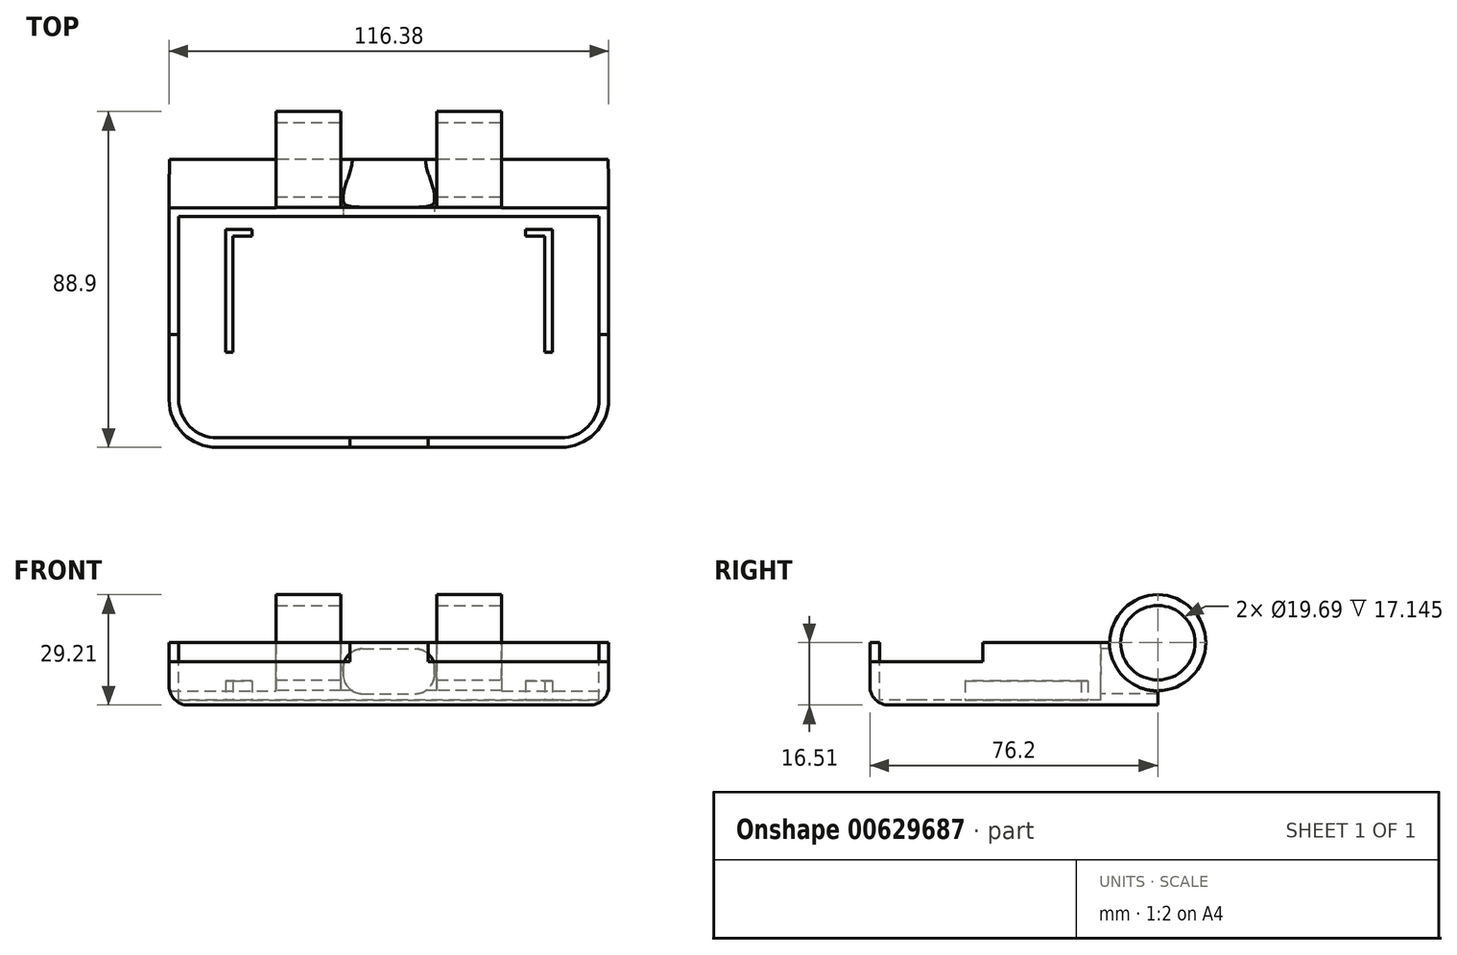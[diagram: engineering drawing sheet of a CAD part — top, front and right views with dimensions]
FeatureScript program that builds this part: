
annotation { "Feature Type Name" : "Feature", "Feature Type Description" : "" }
export const myFeature = defineFeature(function(context is Context, id is Id, definition is map)
    precondition{}
    {
        {
            var Q0;
            Q0=qCreatedBy(makeId("Top.planeOp"),FACE);
            var sketch = newSketch(context, id + "F0", { "sketchPlane" : qUnion([Q0])});
            skLineSegment(sketch, "E0.bottom", {"start": v(58.2, 38.1) * mm, "end": v(-58.2, 38.1) * mm});
            skLineSegment(sketch, "E0.top", {"start": v(58.2, -38.1) * mm, "end": v(-58.2, -38.1) * mm});
            skLineSegment(sketch, "E0.left", {"start": v(58.2, 38.1) * mm, "end": v(58.2, -38.1) * mm});
            skLineSegment(sketch, "E0.right", {"start": v(-58.2, 38.1) * mm, "end": v(-58.2, -38.1) * mm});
            skPoint(sketch, "E0.middle", {"position": v(0, 0) * mm});
            skSolve(sketch);
        }
        {
            var Q0;
            Q0 = qSketchRegion(id + "F0", true);
            extrude(context, id + "F1", {"entities" : qUnion([Q0]), "oppositeDirection" : true, "depth" : 16.5 * mm, "offsetDistance" : 25.4 * mm});
        }
        {
            var Q0;
            Q0=qCreatedBy(makeId("Right.planeOp"),FACE);
            var sketch = newSketch(context, id + "F2", { "sketchPlane" : qUnion([Q0])});
            skCircle(sketch, "E1", {"center": v(38.1, 0) * mm, "radius": 12.7 * mm});
            skSolve(sketch);
        }
        {
            var Q0;
            Q0 = qSketchRegion(id + "F2", true);
            extrude(context, id + "F3", {"entities" : qUnion([Q0]), "operationType" : NewBodyOperationType.ADD, "endBound" : BoundingType.SYMMETRIC, "depth" : 127 * mm, "offsetDistance" : 25.4 * mm});
        }
        {
            var Q0;
            Q0=makeQuery(id+"F1.opExtrude","SWEPT_EDGE",EDGE,{"disambiguationData":[OSD([sQuery(id+"F0.wireOp",EDGE,"E0.top"),sQuery(id+"F0.wireOp",EDGE,"E0.right")])]});
            var Q1;
            Q1=makeQuery(id+"F1.opExtrude","SWEPT_EDGE",EDGE,{"disambiguationData":[OSD([sQuery(id+"F0.wireOp",EDGE,"E0.top"),sQuery(id+"F0.wireOp",EDGE,"E0.left")])]});
            fillet(context, id + "F4", {"entities" : qUnion([Q0, Q1]), "radius" : 12.7 * mm, "tangentPropagation" : true, "allowEdgeOverflow" : false});
        }
        {
            var Q0;
            Q0=qCreatedBy(makeId("Top.planeOp"),FACE);
            var sketch = newSketch(context, id + "F5", { "sketchPlane" : qUnion([Q0])});
            skLineSegment(sketch, "E2.0", {"start": v(63.5, 50.8) * mm, "end": v(63.5, 25.4) * mm, "construction": true});
            skLineSegment(sketch, "E3", {"start": v(-63.5, 38.1) * mm, "end": v(0, 38.1) * mm});
            skLineSegment(sketch, "E4", {"start": v(0, 38.1) * mm, "end": v(63.5, 38.1) * mm});
            skLineSegment(sketch, "E5", {"start": v(63.5, 38.1) * mm, "end": v(63.5, 50.86) * mm});
            skLineSegment(sketch, "E6", {"start": v(63.5, 50.86) * mm, "end": v(29.85, 50.86) * mm});
            skLineSegment(sketch, "E7", {"start": v(29.85, 50.86) * mm, "end": v(29.85, 47.94) * mm});
            skLineSegment(sketch, "E8", {"start": v(29.85, 47.94) * mm, "end": v(0, 47.94) * mm});
            skLineSegment(sketch, "E9", {"start": v(0, 47.94) * mm, "end": v(-29.85, 47.94) * mm});
            skLineSegment(sketch, "E10", {"start": v(-29.85, 47.94) * mm, "end": v(-29.85, 50.86) * mm});
            skLineSegment(sketch, "E11", {"start": v(-29.85, 50.86) * mm, "end": v(-63.5, 50.86) * mm});
            skLineSegment(sketch, "E12", {"start": v(-63.5, 50.86) * mm, "end": v(-63.5, 38.1) * mm});
            skSolve(sketch);
        }
        {
            var Q0;
            Q0 = qSketchRegion(id + "F5", true);
            var Q1;
            Q1=sQuery(id+"F5.wireOp",EDGE,"E4");
            revolve(context, id + "F6", {"operationType" : NewBodyOperationType.REMOVE, "entities" : qUnion([Q0]), "axis" : qUnion([Q1]), "revolveType" : RevolveType.FULL, "oppositeDirection" : true});
        }
        {
            var Q0;
            Q0=makeQuery(id+"F1.opExtrude","CAP_EDGE",EDGE,{"disambiguationData":[OSD([sQuery(id+"F0.wireOp",EDGE,"E0.left")])],"isStart":false});
            fillet(context, id + "F7", {"entities" : qUnion([Q0]), "radius" : 5.08 * mm, "tangentPropagation" : true, "allowEdgeOverflow" : false});
        }
        {
            var Q0;
            Q0=makeQuery(id+"F1.opExtrude","CAP_FACE",FACE,{"disambiguationData":[OSD([sQuery(id+"F0.wireOp",EDGE,"E0.bottom"),sQuery(id+"F0.wireOp",EDGE,"E0.top"),sQuery(id+"F0.wireOp",EDGE,"E0.left"),sQuery(id+"F0.wireOp",EDGE,"E0.right")])],"isStart":true});
            var sketch = newSketch(context, id + "F8", { "sketchPlane" : qUnion([Q0])});
            skLineSegment(sketch, "E13.bottom", {"start": v(55.65, 23.05) * mm, "end": v(-55.65, 23.05) * mm});
            skLineSegment(sketch, "E13.top", {"start": v(55.65, -23.05) * mm, "end": v(-55.65, -23.05) * mm, "construction": true});
            skLineSegment(sketch, "E13.left", {"start": v(55.65, 23.05) * mm, "end": v(55.65, -23.05) * mm});
            skLineSegment(sketch, "E13.right", {"start": v(-55.65, 23.05) * mm, "end": v(-55.65, -23.05) * mm});
            skPoint(sketch, "E13.middle", {"position": v(0, 0) * mm});
            skLineSegment(sketch, "E14", {"start": v(-55.65, -23.05) * mm, "end": v(-55.65, -25.4) * mm});
            skLineSegment(sketch, "E15", {"start": v(-45.5, -35.56) * mm, "end": v(45.5, -35.56) * mm});
            skLineSegment(sketch, "E16", {"start": v(55.65, -25.4) * mm, "end": v(55.65, -23.05) * mm});
            skPoint(sketch, "E17.visualSharp", {"position": v(-55.65, -35.56) * mm});
            skArc(sketch, "E17.filletArc", {"start": v(-55.65, -25.4) * mm, "mid": v(-52.68, -32.58) * mm, "end": v(-45.5, -35.56) * mm});
            skPoint(sketch, "E18.visualSharp", {"position": v(55.65, -35.56) * mm});
            skArc(sketch, "E18.filletArc", {"start": v(45.5, -35.56) * mm, "mid": v(52.68, -32.58) * mm, "end": v(55.65, -25.4) * mm});
            skSolve(sketch);
        }
        {
            var Q0;
            Q0 = qSketchRegion(id + "F8", true);
            extrude(context, id + "F9", {"entities" : qUnion([Q0]), "operationType" : NewBodyOperationType.REMOVE, "oppositeDirection" : true, "depth" : 15.24 * mm, "offsetDistance" : 25.4 * mm});
        }
        {
            var Q0;
            Q0=qCreatedBy(makeId("Right.planeOp"),FACE);
            var sketch = newSketch(context, id + "F10", { "sketchPlane" : qUnion([Q0])});
            skArc(sketch, "E19.0", {"start": v(25.4, 0) * mm, "mid": v(47.08, 8.98) * mm, "end": v(38.1, -12.7) * mm, "construction": true});
            skCircle(sketch, "E20", {"center": v(38.1, 0) * mm, "radius": 12.7 * mm});
            skSolve(sketch);
        }
        {
            var Q0;
            Q0 = qSketchRegion(id + "F10", true);
            extrude(context, id + "F11", {"entities" : qUnion([Q0]), "operationType" : NewBodyOperationType.REMOVE, "endBound" : BoundingType.SYMMETRIC, "depth" : 25.4 * mm, "offsetDistance" : 25.4 * mm});
        }
        {
            var Q0;
            Q0=makeQuery(id+"F9.boolean.opBoolean","COPY",FACE,{"derivedFrom":makeQuery(id+"F9.opExtrude","SWEPT_FACE",FACE,{"disambiguationData":[OSD([sQuery(id+"F8.wireOp",EDGE,"E13.bottom")])]})});
            var sketch = newSketch(context, id + "F12", { "sketchPlane" : qUnion([Q0])});
            skLineSegment(sketch, "E21.bottom", {"start": v(-6.99, -1.6) * mm, "end": v(6.99, -1.6) * mm});
            skLineSegment(sketch, "E21.top", {"start": v(-6.99, -13.5) * mm, "end": v(6.99, -13.5) * mm});
            skLineSegment(sketch, "E21.left", {"start": v(-12.07, -6.69) * mm, "end": v(-12.07, -8.42) * mm});
            skLineSegment(sketch, "E21.right", {"start": v(12.07, -6.69) * mm, "end": v(12.07, -8.42) * mm});
            skLineSegment(sketch, "E22.0", {"start": v(55.65, -15.24) * mm, "end": v(-55.65, -15.24) * mm, "construction": true});
            skLineSegment(sketch, "E23", {"start": v(0, -15.24) * mm, "end": v(0, -13.5) * mm, "construction": true});
            skPoint(sketch, "E24.visualSharp", {"position": v(-12.06, -1.6) * mm});
            skArc(sketch, "E24.filletArc", {"start": v(-6.99, -1.6) * mm, "mid": v(-10.58, -3.1) * mm, "end": v(-12.07, -6.69) * mm});
            skPoint(sketch, "E25.visualSharp", {"position": v(12.06, -1.6) * mm});
            skArc(sketch, "E25.filletArc", {"start": v(12.07, -6.69) * mm, "mid": v(10.58, -3.1) * mm, "end": v(6.99, -1.6) * mm});
            skPoint(sketch, "E26.visualSharp", {"position": v(12.06, -13.5) * mm});
            skArc(sketch, "E26.filletArc", {"start": v(6.99, -13.5) * mm, "mid": v(10.58, -12) * mm, "end": v(12.07, -8.42) * mm});
            skPoint(sketch, "E27.visualSharp", {"position": v(-12.06, -13.5) * mm});
            skArc(sketch, "E27.filletArc", {"start": v(-12.07, -8.42) * mm, "mid": v(-10.58, -12) * mm, "end": v(-6.99, -13.5) * mm});
            skSolve(sketch);
        }
        {
            var Q0;
            Q0 = qSketchRegion(id + "F12", true);
            extrude(context, id + "F13", {"entities" : qUnion([Q0]), "operationType" : NewBodyOperationType.REMOVE, "oppositeDirection" : true, "depth" : 25.4 * mm, "offsetDistance" : 25.4 * mm});
        }
        {
            var Q0;
            Q0=makeQuery(id+"F9.boolean.opBoolean","COPY",FACE,{"derivedFrom":makeQuery(id+"F9.opExtrude","CAP_FACE",FACE,{"disambiguationData":[OSD([sQuery(id+"F8.wireOp",EDGE,"E13.bottom"),sQuery(id+"F8.wireOp",EDGE,"E13.left"),sQuery(id+"F8.wireOp",EDGE,"E13.right"),sQuery(id+"F8.wireOp",EDGE,"E14"),sQuery(id+"F8.wireOp",EDGE,"E15"),sQuery(id+"F8.wireOp",EDGE,"E16"),sQuery(id+"F8.wireOp",EDGE,"E17.filletArc"),sQuery(id+"F8.wireOp",EDGE,"E18.filletArc")])],"isStart":false})});
            var sketch = newSketch(context, id + "F14", { "sketchPlane" : qUnion([Q0])});
            skLineSegment(sketch, "E28", {"start": v(-41.28, 17.78) * mm, "end": v(-36.2, 17.78) * mm});
            skLineSegment(sketch, "E29", {"start": v(-36.2, 17.78) * mm, "end": v(36.2, 17.78) * mm, "construction": true});
            skLineSegment(sketch, "E30", {"start": v(36.2, 17.78) * mm, "end": v(41.28, 17.78) * mm});
            skLineSegment(sketch, "E31", {"start": v(41.28, 17.78) * mm, "end": v(41.28, -12.86) * mm});
            skLineSegment(sketch, "E32", {"start": v(41.28, -12.86) * mm, "end": v(43.26, -12.86) * mm});
            skLineSegment(sketch, "E33", {"start": v(43.26, -12.86) * mm, "end": v(43.26, 19.56) * mm});
            skLineSegment(sketch, "E34", {"start": v(43.26, 19.56) * mm, "end": v(36.2, 19.56) * mm});
            skLineSegment(sketch, "E35", {"start": v(36.2, 19.56) * mm, "end": v(36.2, 17.78) * mm});
            skLineSegment(sketch, "E36", {"start": v(-36.2, 17.78) * mm, "end": v(-36.2, 19.56) * mm});
            skLineSegment(sketch, "E37", {"start": v(-36.2, 19.56) * mm, "end": v(-43.26, 19.56) * mm});
            skLineSegment(sketch, "E38", {"start": v(-43.26, 19.56) * mm, "end": v(-43.26, -12.86) * mm});
            skLineSegment(sketch, "E39", {"start": v(-43.26, -12.86) * mm, "end": v(-41.28, -12.86) * mm});
            skLineSegment(sketch, "E40", {"start": v(-41.28, -12.86) * mm, "end": v(-41.28, 17.78) * mm});
            skLineSegment(sketch, "E41", {"start": v(0, 0) * mm, "end": v(0, 17.78) * mm, "construction": true});
            skSolve(sketch);
        }
        {
            var Q0;
            Q0 = qSketchRegion(id + "F14", true);
            extrude(context, id + "F15", {"entities" : qUnion([Q0]), "operationType" : NewBodyOperationType.ADD, "depth" : 5.08 * mm, "offsetDistance" : 25.4 * mm});
        }
        {
            var Q0;
            Q0=makeQuery(id+"F1.opExtrude","CAP_FACE",FACE,{"disambiguationData":[OSD([sQuery(id+"F0.wireOp",EDGE,"E0.bottom"),sQuery(id+"F0.wireOp",EDGE,"E0.top"),sQuery(id+"F0.wireOp",EDGE,"E0.left"),sQuery(id+"F0.wireOp",EDGE,"E0.right")])],"isStart":true});
            var sketch = newSketch(context, id + "F16", { "sketchPlane" : qUnion([Q0])});
            skLineSegment(sketch, "E42.bottom", {"start": v(-58.2, -8.24) * mm, "end": v(-10.34, -8.24) * mm});
            skLineSegment(sketch, "E42.top", {"start": v(-58.2, -38.1) * mm, "end": v(-10.34, -38.1) * mm});
            skLineSegment(sketch, "E42.left", {"start": v(-58.2, -8.24) * mm, "end": v(-58.2, -38.1) * mm});
            skLineSegment(sketch, "E42.right", {"start": v(-10.34, -8.24) * mm, "end": v(-10.34, -38.1) * mm});
            skLineSegment(sketch, "E43.bottom", {"start": v(58.2, -8.24) * mm, "end": v(10.34, -8.24) * mm});
            skLineSegment(sketch, "E43.top", {"start": v(58.2, -38.1) * mm, "end": v(10.34, -38.1) * mm});
            skLineSegment(sketch, "E43.left", {"start": v(58.2, -8.24) * mm, "end": v(58.2, -38.1) * mm});
            skLineSegment(sketch, "E43.right", {"start": v(10.34, -8.24) * mm, "end": v(10.34, -38.1) * mm});
            skLineSegment(sketch, "E44", {"start": v(-10.34, -8.24) * mm, "end": v(10.34, -8.24) * mm, "construction": true});
            skLineSegment(sketch, "E45", {"start": v(0, 0) * mm, "end": v(0, -8.24) * mm, "construction": true});
            skSolve(sketch);
        }
        {
            var Q0;
            Q0 = qSketchRegion(id + "F16", true);
            extrude(context, id + "F17", {"entities" : qUnion([Q0]), "operationType" : NewBodyOperationType.REMOVE, "oppositeDirection" : true, "depth" : 5.08 * mm, "offsetDistance" : 25.4 * mm});
        }
    });
